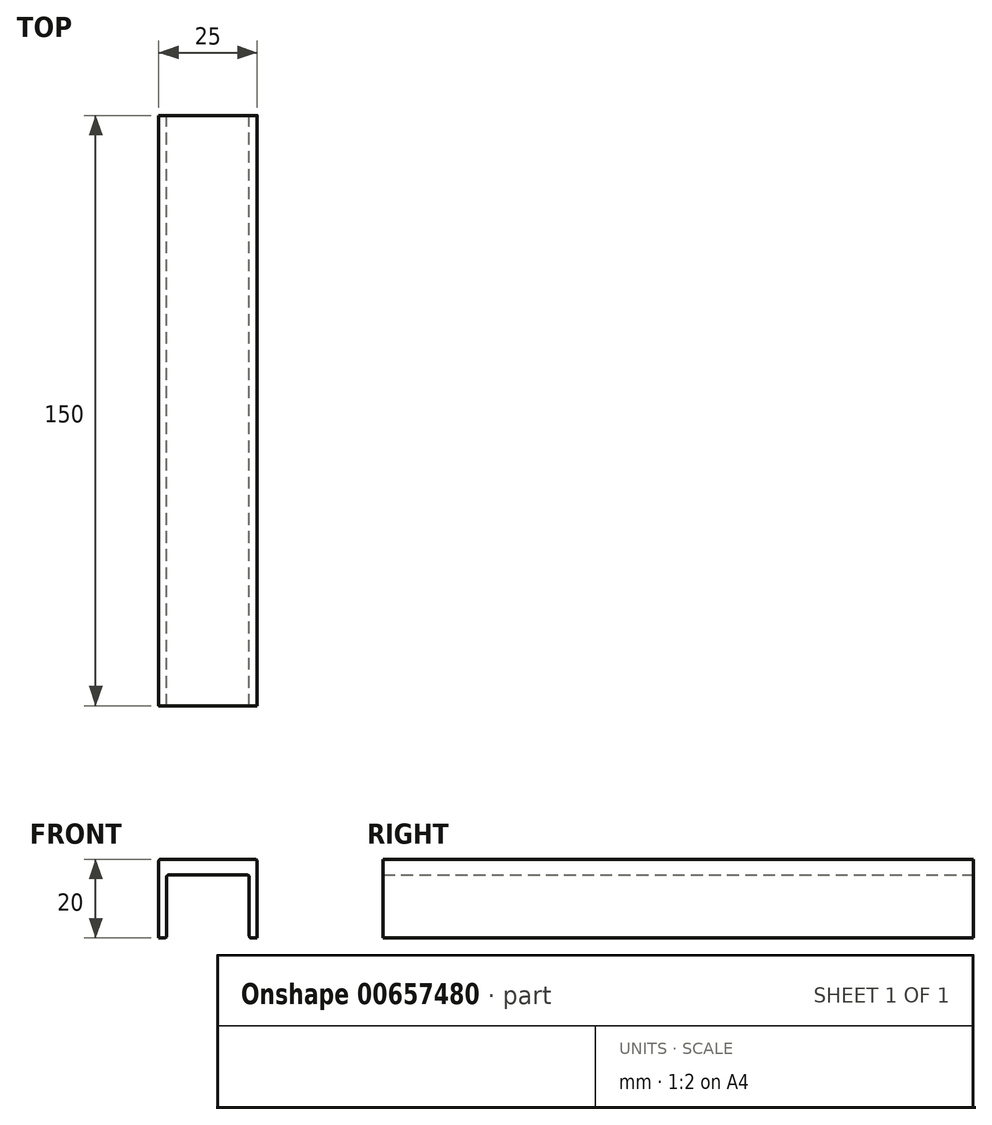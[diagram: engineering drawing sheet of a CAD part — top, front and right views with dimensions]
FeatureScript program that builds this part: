
annotation { "Feature Type Name" : "Feature", "Feature Type Description" : "" }
export const myFeature = defineFeature(function(context is Context, id is Id, definition is map)
    precondition{}
    {
        {
            var Q0;
            Q0=qCreatedBy(makeId("Front.planeOp"),FACE);
            var sketch = newSketch(context, id + "F0", { "sketchPlane" : qUnion([Q0])});
            skLineSegment(sketch, "E0", {"start": v(0, 20) * mm, "end": v(0, 0) * mm});
            skLineSegment(sketch, "E1", {"start": v(0, 0) * mm, "end": v(2, 0) * mm});
            skLineSegment(sketch, "E2", {"start": v(2, 0) * mm, "end": v(2, 16) * mm});
            skLineSegment(sketch, "E3", {"start": v(23, 16) * mm, "end": v(23, 0) * mm});
            skLineSegment(sketch, "E4", {"start": v(23, 0) * mm, "end": v(25, 0) * mm});
            skLineSegment(sketch, "E5", {"start": v(25, 0) * mm, "end": v(25, 20) * mm});
            skLineSegment(sketch, "E6", {"start": v(25, 20) * mm, "end": v(0, 20) * mm});
            skLineSegment(sketch, "E7", {"start": v(2, 16) * mm, "end": v(23, 16) * mm});
            skSolve(sketch);
        }
        {
            var Q0;
            Q0=qSketchRegion(id+"F0",true);
            extrude(context, id + "F1", {"entities" : qUnion([Q0]), "endBound" : BoundingType.SYMMETRIC, "depth" : 150 * mm, "offsetDistance" : 25 * mm});
        }
        {
            var Q0;
            Q0=makeQuery(id+"F1.opExtrude","SWEPT_FACE",FACE,{"disambiguationData":[OSD([sQuery(id+"F0.wireOp",EDGE,"E6")])]});
            var sketch = newSketch(context, id + "F2", { "sketchPlane" : qUnion([Q0])});
            skCircle(sketch, "E8", {"center": v(12.5, 0) * mm, "radius": 2.5 * mm});
            skSolve(sketch);
        }
        {
            var Q0;
            Q0=makeQuery(id+"F1.opExtrude","SWEPT_EDGE",EDGE,{"disambiguationData":[OSD([sQuery(id+"F0.wireOp",EDGE,"E0"),sQuery(id+"F0.wireOp",EDGE,"E6")])]});
            var Q1;
            Q1=makeQuery(id+"F1.opExtrude","SWEPT_EDGE",EDGE,{"disambiguationData":[OSD([sQuery(id+"F0.wireOp",EDGE,"E5"),sQuery(id+"F0.wireOp",EDGE,"E6")])]});
            var Q2;
            Q2=makeQuery(id+"F1.opExtrude","SWEPT_EDGE",EDGE,{"disambiguationData":[OSD([sQuery(id+"F0.wireOp",EDGE,"E2"),sQuery(id+"F0.wireOp",EDGE,"5D46qFQe-UmXA-BcV9-RR1S-OxmLbhrvSHBb")])]});
            var Q3;
            Q3=makeQuery(id+"F1.opExtrude","SWEPT_EDGE",EDGE,{"disambiguationData":[OSD([sQuery(id+"F0.wireOp",EDGE,"5D46qFQe-UmXA-BcV9-RR1S-OxmLbhrvSHBb"),sQuery(id+"F0.wireOp",EDGE,"E3")])]});
            fillet(context, id + "F3", {"entities" : qUnion([Q0, Q1, Q2, Q3]), "radius" : .5 * mm, "tangentPropagation" : true, "allowEdgeOverflow" : false});
        }
    });
